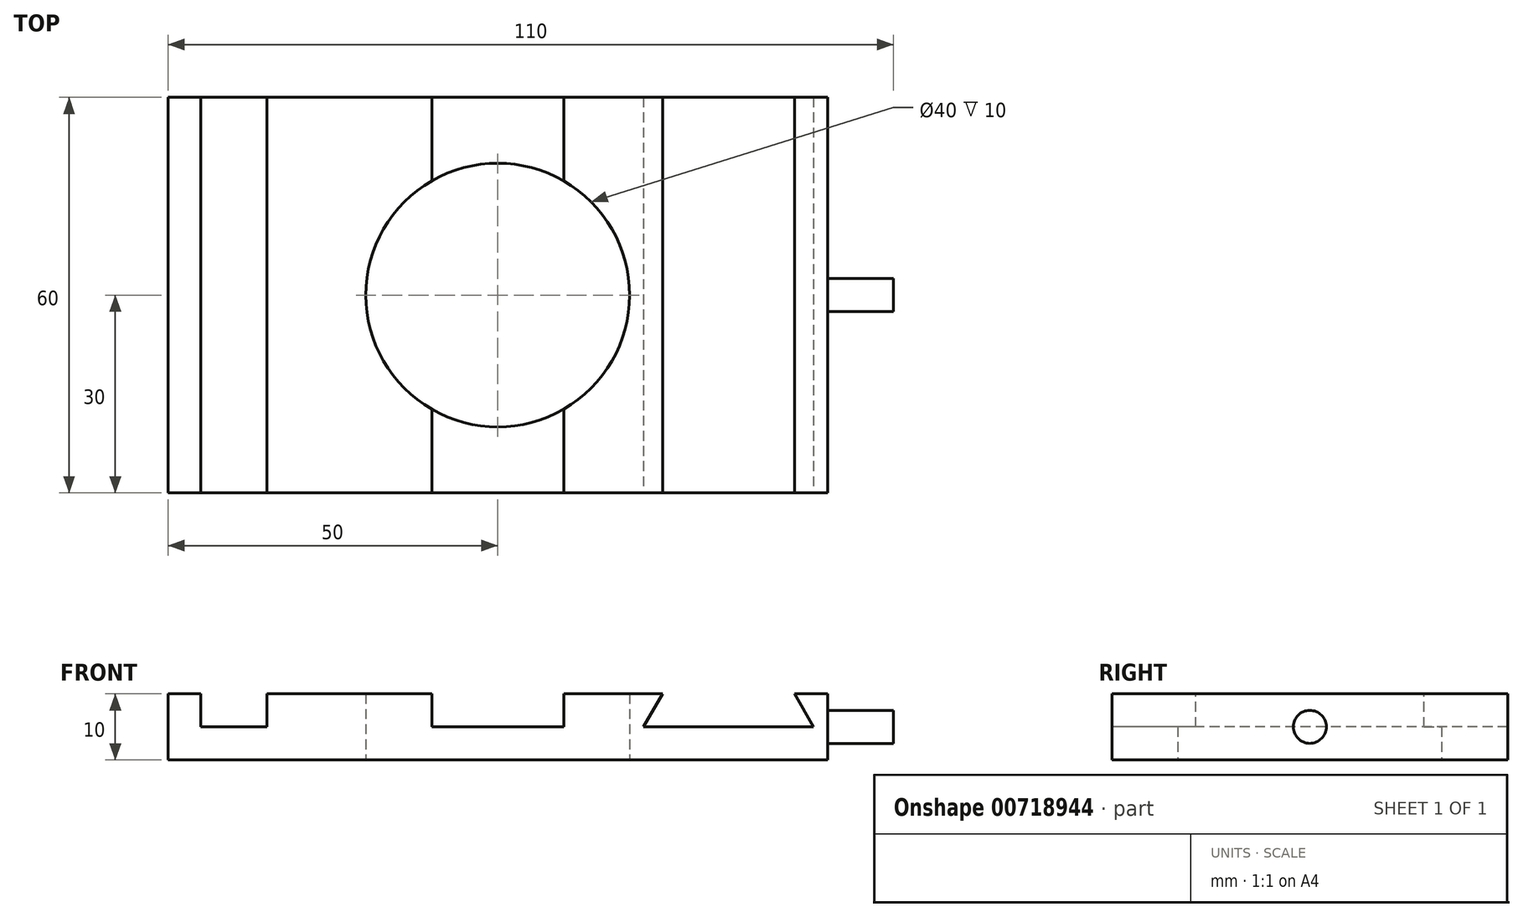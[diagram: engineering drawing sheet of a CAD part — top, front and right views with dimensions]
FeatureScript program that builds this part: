
annotation { "Feature Type Name" : "Feature", "Feature Type Description" : "" }
export const myFeature = defineFeature(function(context is Context, id is Id, definition is map)
    precondition{}
    {
        {
            var Q0;
            Q0=qCreatedBy(makeId("Top.planeOp"),FACE);
            var sketch = newSketch(context, id + "F0", { "sketchPlane" : qUnion([Q0])});
            skLineSegment(sketch, "E0.bottom", {"start": v(50, 30) * mm, "end": v(-50, 30) * mm});
            skLineSegment(sketch, "E0.top", {"start": v(50, -30) * mm, "end": v(-50, -30) * mm});
            skLineSegment(sketch, "E0.left", {"start": v(50, 30) * mm, "end": v(50, -30) * mm});
            skLineSegment(sketch, "E0.right", {"start": v(-50, 30) * mm, "end": v(-50, -30) * mm});
            skPoint(sketch, "E0.middle", {"position": v(0, 0) * mm});
            skCircle(sketch, "E1", {"center": v(0, 0) * mm, "radius": 20 * mm});
            skSolve(sketch);
        }
        {
            var Q0;
            Q0=makeQuery(id+"F0.imprint","IMPRINT",FACE,{"disambiguationData":[TD([[makeQuery(id+"F0.imprint","IMPRINT",EDGE,{"derivedFrom":sQuery(id+"F0.wireOp",EDGE,"E0.bottom")}),1.0]])]});
            extrude(context, id + "F1", {"entities" : qUnion([Q0]), "depth" : 10 * mm, "offsetDistance" : 25.4 * mm});
        }
        {
            var Q0;
            Q0=makeQuery(id+"F1.opExtrude","CAP_FACE",FACE,{"disambiguationData":[OSD([sQuery(id+"F0.wireOp",EDGE,"E0.bottom"),sQuery(id+"F0.wireOp",EDGE,"E0.top"),sQuery(id+"F0.wireOp",EDGE,"E0.left"),sQuery(id+"F0.wireOp",EDGE,"E0.right"),sQuery(id+"F0.wireOp",EDGE,"E1")])],"isStart":false});
            var sketch = newSketch(context, id + "F2", { "sketchPlane" : qUnion([Q0])});
            skLineSegment(sketch, "E2.bottom", {"start": v(-45, 30) * mm, "end": v(-35, 30) * mm});
            skLineSegment(sketch, "E2.top", {"start": v(-45, -30) * mm, "end": v(-35, -30) * mm});
            skLineSegment(sketch, "E2.left", {"start": v(-45, 30) * mm, "end": v(-45, -30) * mm});
            skLineSegment(sketch, "E2.right", {"start": v(-35, 30) * mm, "end": v(-35, -30) * mm});
            skLineSegment(sketch, "E3", {"start": v(-10, 30) * mm, "end": v(-10, -30) * mm});
            skLineSegment(sketch, "E4", {"start": v(-10, -30) * mm, "end": v(10, -30) * mm});
            skLineSegment(sketch, "E5", {"start": v(10, -30) * mm, "end": v(10, 30) * mm});
            skLineSegment(sketch, "E6", {"start": v(10, 30) * mm, "end": v(-10, 30) * mm});
            skPoint(sketch, "E7", {"position": v(0, 0) * mm});
            skLineSegment(sketch, "E8", {"start": v(0, 30) * mm, "end": v(0, -30) * mm, "construction": true});
            skSolve(sketch);
        }
        {
            var Q0;
            Q0=makeQuery(id+"F2.imprint","IMPRINT",FACE,{"disambiguationData":[TD([[makeQuery(id+"F2.imprint","IMPRINT",EDGE,{"derivedFrom":sQuery(id+"F2.wireOp",EDGE,"E2.bottom")}),1.0]])]});
            var Q1;
            {var subQ0=sQuery(id+"F2.wireOp",EDGE,"E6");Q1=makeQuery(id+"F2.imprint","IMPRINT",FACE,{"disambiguationData":[TD([[makeQuery(id+"F2.imprint","IMPRINT",EDGE,{"derivedFrom":subQ0}),1.0]])]});}
            var Q2;
            {var subQ0=sQuery(id+"F2.wireOp",EDGE,"E4");Q2=makeQuery(id+"F2.imprint","IMPRINT",FACE,{"disambiguationData":[TD([[makeQuery(id+"F2.imprint","IMPRINT",EDGE,{"derivedFrom":subQ0}),-1.0]])]});}
            extrude(context, id + "F3", {"entities" : qUnion([Q0, Q1, Q2]), "operationType" : NewBodyOperationType.REMOVE, "oppositeDirection" : true, "depth" : 5 * mm, "offsetDistance" : 25 * mm});
        }
        {
            var Q0;
            Q0=makeQuery(id+"F1.opExtrude","SWEPT_FACE",FACE,{"disambiguationData":[OSD([sQuery(id+"F0.wireOp",EDGE,"E0.top")])]});
            var sketch = newSketch(context, id + "F4", { "sketchPlane" : qUnion([Q0])});
            skLineSegment(sketch, "E9", {"start": v(25, 10) * mm, "end": v(22.11, 5) * mm});
            skLineSegment(sketch, "E10", {"start": v(22.11, 5) * mm, "end": v(47.89, 5) * mm});
            skLineSegment(sketch, "E11", {"start": v(47.89, 5) * mm, "end": v(45, 10) * mm});
            skLineSegment(sketch, "E12", {"start": v(45, 10) * mm, "end": v(25, 10) * mm});
            skLineSegment(sketch, "E13", {"start": v(35, 5) * mm, "end": v(35, 10) * mm, "construction": true});
            skSolve(sketch);
        }
        {
            var Q0;
            Q0 = qSketchRegion(id + "F4", true);
            extrude(context, id + "F5", {"entities" : qUnion([Q0]), "operationType" : NewBodyOperationType.REMOVE, "endBound" : BoundingType.THROUGH_ALL, "oppositeDirection" : true, "depth" : 25 * mm, "offsetDistance" : 25 * mm});
        }
        {
            var Q0;
            Q0=makeQuery(id+"F1.opExtrude","SWEPT_FACE",FACE,{"disambiguationData":[OSD([sQuery(id+"F0.wireOp",EDGE,"E0.left")])]});
            var sketch = newSketch(context, id + "F6", { "sketchPlane" : qUnion([Q0])});
            skCircle(sketch, "E14", {"center": v(0, 5) * mm, "radius": 2.5 * mm});
            skPoint(sketch, "E14.centerSnap0", {"position": v(-30, 5) * mm});
            skPoint(sketch, "E14.centerSnap1", {"position": v(0, 10) * mm});
            skSolve(sketch);
        }
        {
            var Q0;
            Q0 = qSketchRegion(id + "F6", true);
            extrude(context, id + "F7", {"entities" : qUnion([Q0]), "operationType" : NewBodyOperationType.ADD, "depth" : 10 * mm, "offsetDistance" : 25 * mm});
        }
    });
